# Revit family: QHC
name_source: partatom
category: Lighting Fixtures
revit_build: Autodesk Revit 2013 (Build: 20130531_2115(x64)
units: mm (PartAtom-declared; Revit-internal decimal feet)

## types (1)
- QHC
    Apparent Load = 150 VA
    Color Filter = 16777215
    Default Elevation = 48"
    Description = Modular Chassis LED High-Bay
    Dimming Lamp Color Temperature Shift = <None>
    Emit Shape Visible in Rendering = No
    Emit from Rectangle Length = 8 1/2"
    Emit from Rectangle Width = 10 1/2"
    Glass = Hubbell - White Glass
    Housing Material = Hubbell-Paint-White
    Lamp = 36, 48, 60, 120, 180 Chip Board LEDs
    Load Classification = Lighting
    Manufacturer = Hubbell Industrial Lighting
    Manufacturer Fax = 866-898-0131
    Model = QHC Series
    Nominal Watts = 135 W
    Photometric Web File = generic.ies
    Photometric Web Link = http://www.hubbellindustrial.com
    Power Factor = 0.9
    Product Documentation Link = http://cdn.hubbellindustrial.com
    Product Page URL = http://www.hubbellindustrial.com
    Tilt Angle = -90.00°
    URL = http://www.hubbellindustrial.com
    Voltage = 120 V
    Warranty = Five year warranty
    Wattage Comments = 135w

## geometry (parser evidence)
native form markers: Sweep x1
no freeform markers — native parametric forms only
